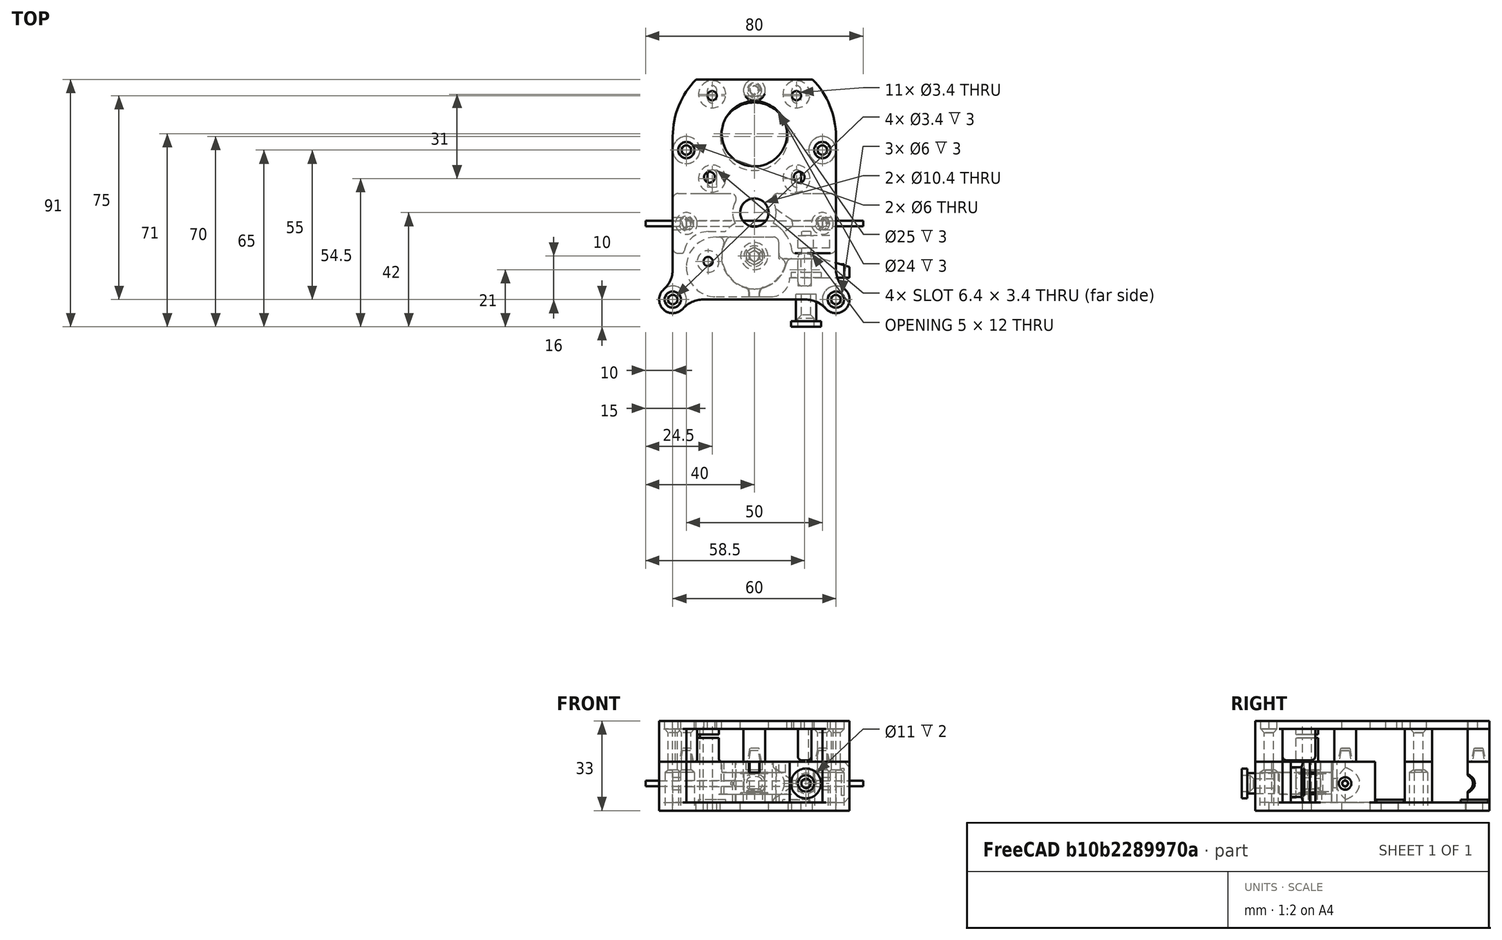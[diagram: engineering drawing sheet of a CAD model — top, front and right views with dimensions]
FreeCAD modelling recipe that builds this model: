
FCSTD DOCUMENT  (FreeCAD 0.14R3700 (Git))
Label: Extruder
License: CC-BY 3.0
LicenseURL: http://creativecommons.org/licenses/by/3.0/
objects: Part::Cylinder×75, Part::Cut×45, Part::MultiFuse×24, Part::Box×20, Part::Cone×12, Mesh::Feature×11, Part::Fillet×7, Part::Chamfer×6, PartDesign::Pad×5, Part::Wedge×2, Sketcher::SketchObject×1
note: 202 computed .brp shape members not serialized (recipe doc carries the construction recipe); baked Part::Feature solids carry a one-line shape summary decoded from their .brp

FEATURE [Part::Box] Box  label="DeltaCubeNema17"
  Height = 3
  Length = 44
  Placement = pos=(-22,21,0) rot=(0,0,1;0rad)
  Width = 10
FEATURE [Part::Cylinder] Cylinder012  label="DeltaCylinderSmallGearTop"
  Angle = 360
  Height = 3
  Placement = pos=(0,1,30) rot=(0,0,1;0rad)
  Radius = 12
FEATURE [Part::Cylinder] Cylinder015
  Angle = 360
  Height = 20
  Placement = pos=(15.5,14,0) rot=(0,0,1;0rad)
  Radius = 1.7
FEATURE [Part::Cylinder] Cylinder016
  Angle = 360
  Height = 20
  Placement = pos=(-15.5,-17,0) rot=(0,0,1;0rad)
  Radius = 1.7
FEATURE [Part::Cylinder] Cylinder017
  Angle = 360
  Height = 20
  Placement = pos=(15.5,-14,0) rot=(0,0,1;0rad)
  Radius = 1.7
FEATURE [Part::Box] Box004  label="Cube"
  Height = 20
  Length = 3.4
  Placement = pos=(13.8,14,0) rot=(0,0,1;0rad)
  Width = 3
FEATURE [Part::Box] Box005  label="Cube051"
  Height = 20
  Length = 3.4
  Placement = pos=(-17.2,-17,0) rot=(0,0,1;0rad)
  Width = 3
FEATURE [Part::Box] Box006  label="Cube052"
  Height = 20
  Length = 3.4
  Placement = pos=(-17.2,14,0) rot=(0,0,1;0rad)
  Width = 3
FEATURE [Part::Box] Box007  label="Cube053"
  Height = 20
  Length = 3.4
  Placement = pos=(13.8,-17,0) rot=(0,0,1;0rad)
  Width = 3
FEATURE [Part::Cylinder] Cylinder018
  Angle = 360
  Height = 20
  Placement = pos=(-15.5,17,0) rot=(0,0,1;0rad)
  Radius = 1.7
FEATURE [Part::Cylinder] Cylinder019
  Angle = 360
  Height = 20
  Placement = pos=(15.5,17,0) rot=(0,0,1;0rad)
  Radius = 1.7
FEATURE [Part::Cylinder] Cylinder020
  Angle = 360
  Height = 20
  Placement = pos=(-15.5,-14,0) rot=(0,0,1;0rad)
  Radius = 1.7
FEATURE [Part::Cylinder] Cylinder021
  Angle = 360
  Height = 20
  Placement = pos=(15.5,-17,0) rot=(0,0,1;0rad)
  Radius = 1.7
FEATURE [Part::Box] Box008  label="CubeBaseTop"
  Height = 3
  Length = 60
  Placement = pos=(-30,-60,30) rot=(0,0,1;0rad)
  Width = 60
FEATURE [Part::Cylinder] Cylinder034  label="DO_NOT_PRINT-Filament"
  Angle = 360
  Height = 80
  Placement = pos=(-40,-32,10) rot=(0,1,0;1.5708rad)
  Radius = 1
FEATURE [Part::Box] Box009  label="PressureCube"
  Height = 15
  Length = 50
  Placement = pos=(-25,-59,3) rot=(0,0,1;0rad)
  Width = 22
FEATURE [Part::Box] Box011  label="FilementHolder"
  Height = 15
  Length = 60
  Placement = pos=(-30,-43,3) rot=(0,0,1;0rad)
  Width = 22
FEATURE [Part::Box] Box012  label="DeltaCube"
  Height = 15
  Length = 16
  Placement = pos=(9,-45,3) rot=(0,0,1;0rad)
  Width = 9
FEATURE [Part::Cylinder] Cylinder040  label="DeltaCylinderSpringPocket"
  Angle = 360
  Height = 2
  Placement = pos=(19,-50,10) rot=(1,0,0;1.5708rad)
  Radius = 5.5
FEATURE [Part::Cylinder] Cylinder041  label="DeltaCylinderSpringNutM4"
  Angle = 360
  Height = 7
  Placement = pos=(19,-45,10) rot=(1,0,0;1.5708rad)
  Radius = 2
FEATURE [Part::Box] Box013  label="DeltaCube001"
  Height = 11
  Length = 5.8
  Placement = pos=(16,-41,7) rot=(0,0,1;0rad)
  Width = 4.5
FEATURE [Part::Cylinder] Cylinder042  label="DeltaCylinder002"
  Angle = 360
  Height = 12
  Placement = pos=(19,-35,10) rot=(1,0,0;1.5708rad)
  Radius = 1.7
FEATURE [Part::Cylinder] Cylinder044  label="DeltaCylinderBearing"
  Angle = 360
  Height = 12
  Placement = pos=(0,-44,6) rot=(0,0,1;0rad)
  Radius = 12.1
FEATURE [Part::Cylinder] Cylinder045  label="CylinderBearingID"
  Angle = 360
  Height = 10.7
  Placement = pos=(0,-44,3) rot=(0,0,1;0rad)
  Radius = 3.8
FEATURE [Part::Cylinder] Cylinder046  label="CylinderBearingBottom"
  Angle = 360
  Height = 0.5
  Placement = pos=(0,-44,6) rot=(0,0,1;0rad)
  Radius = 5
FEATURE [Part::Box] Box014  label="DeltaCubeNema17Top"
  Height = 3
  Length = 44
  Placement = pos=(-22,21,30) rot=(0,0,1;0rad)
  Width = 10
FEATURE [Part::Cylinder] Cylinder047  label="Cylinder043"
  Angle = 360
  Height = 18
  Placement = pos=(30,-60,0) rot=(0,0,-1;0.785398rad)
  Radius = 5
FEATURE [Part::Cylinder] Cylinder048  label="Cylinder044"
  Angle = 360
  Height = 18
  Placement = pos=(-30,-60,0) rot=(0,0,1;3.92699rad)
  Radius = 5
FEATURE [Part::Cylinder] Cylinder049  label="Cylinder045"
  Angle = 360
  Height = 18
  Placement = pos=(25,-5,0) rot=(0,0,1;0rad)
  Radius = 5
FEATURE [Part::Cylinder] Cylinder050  label="Cylinder046"
  Angle = 360
  Height = 18
  Placement = pos=(-25,-5,0) rot=(0,0,1;0rad)
  Radius = 5
FEATURE [Part::Cylinder] Cylinder051  label="AlignmentCylinderNema17"
  Angle = 360
  Height = 18
  Placement = pos=(0,17,0) rot=(0,0,1;0rad)
  Radius = 4
FEATURE [Part::Cylinder] Cylinder052  label="DeltaCylinder005"
  Angle = 360
  Height = 3
  Placement = pos=(30,-60,30) rot=(0,0,1;0rad)
  Radius = 3
FEATURE [Part::Cylinder] Cylinder053  label="DeltaCylinder006"
  Angle = 360
  Height = 3
  Placement = pos=(-30,-60,30) rot=(0,0,1;0rad)
  Radius = 3
FEATURE [Part::Cylinder] Cylinder054  label="DeltaCylinder007"
  Angle = 360
  Height = 3
  Placement = pos=(25,-5,30) rot=(0,0,1;0rad)
  Radius = 3
FEATURE [Part::Cylinder] Cylinder055  label="DeltaCylinder008"
  Angle = 360
  Height = 3
  Placement = pos=(-25,-5,30) rot=(0,0,1;0rad)
  Radius = 3
FEATURE [Part::Cylinder] Cylinder056  label="Cylinder048"
  Angle = 360
  Height = 15
  Placement = pos=(30,-60,18) rot=(0,0,-1;0.785398rad)
  Radius = 5
FEATURE [Part::Cylinder] Cylinder057  label="Cylinder049"
  Angle = 360
  Height = 15
  Placement = pos=(-30,-60,18) rot=(0,0,1;3.75246rad)
  Radius = 5
FEATURE [Part::Cylinder] Cylinder058  label="Cylinder050"
  Angle = 360
  Height = 15
  Placement = pos=(25,-5,18) rot=(0,0,1;0rad)
  Radius = 5
FEATURE [Part::Cylinder] Cylinder059  label="Cylinder051"
  Angle = 360
  Height = 15
  Placement = pos=(-25,-5,18) rot=(0,0,1;0rad)
  Radius = 5
FEATURE [Part::Cylinder] Cylinder060  label="Cylinder052"
  Angle = 360
  Height = 15
  Placement = pos=(0,17,18) rot=(0,0,1;0rad)
  Radius = 4
FEATURE [Part::Cylinder] Cylinder061  label="CylinderBaseBottom"
  Angle = 360
  Height = 3
  Radius = 30
FEATURE [Part::Cylinder] Cylinder062  label="CylinderBaseTop"
  Angle = 360
  Height = 3
  Placement = pos=(0,0,30) rot=(0,0,1;0rad)
  Radius = 30
FEATURE [Part::Cylinder] Cylinder065  label="DeltaCylinder010"
  Angle = 360
  Height = 15
  Placement = pos=(-17,-44,3) rot=(0,0,1;0rad)
  Radius = 9
FEATURE [Part::Cylinder] Cylinder066  label="DeltaCylinder011"
  Angle = 360
  Height = 15
  Placement = pos=(0,-44,3) rot=(0,0,1;0rad)
  Radius = 14
FEATURE [Part::Cylinder] Cylinder067  label="DeltaCylinder012"
  Angle = 360
  Height = 15
  Placement = pos=(0,-28,3) rot=(0,0,1;0rad)
  Radius = 8
FEATURE [Part::Box] Box015  label="DeltaBox"
  Height = 15
  Length = 17
  Placement = pos=(-17,-43,3) rot=(0,0,1;0rad)
  Width = 8
FEATURE [Part::Cut] Cut028
  Base = -> Box011
  Tool = -> Cylinder067
FEATURE [Part::Cut] Cut029
  Base = -> Cut028
  Tool = -> Cylinder066
FEATURE [Part::Cut] Cut030
  Base = -> Cut029
  Tool = -> Cylinder065
FEATURE [Part::Cut] Cut031
  Base = -> Cut030
  Tool = -> Box015
FEATURE [Part::Cut] Cut032
  Base = -> Cut031
  Tool = -> Box013
FEATURE [Part::Cut] Cut033
  Base = -> Cut032
  Tool = -> Cylinder042
FEATURE [Part::Cylinder] Cylinder068  label="DeltaCylinder013"
  Angle = 360
  Height = 80
  Placement = pos=(-40,-32,10) rot=(0,1,0;1.5708rad)
  Radius = 1.1
FEATURE [Part::Cut] Cut034
  Base = -> Cut033
  Tool = -> Cylinder068
FEATURE [Part::Fillet] Fillet002
  Base = -> Cut034
  Edges = 6 edges r=2: [Edge1,Edge4,Edge19,Edge30,Edge44,Edge57]
FEATURE [Part::Fillet] Fillet003
  Base = -> Fillet002
  Edges = 3 edges r=1: [Edge34,Edge35,Edge39]
FEATURE [Part::Cylinder] Cylinder070  label="DeltaCylinder014"
  Angle = 360
  Height = 5
  Placement = pos=(-30,-32,10) rot=(0,1,0;1.5708rad)
  Radius = 2.3
FEATURE [Part::Cylinder] Cylinder071  label="DeltaCylinder015"
  Angle = 360
  Height = 5
  Placement = pos=(25,-32,10) rot=(0,1,0;1.5708rad)
  Radius = 2.3
FEATURE [Part::Cut] Cut035
  Base = -> Fillet003
  Tool = -> Cylinder070
FEATURE [Part::Cut] Cut036
  Base = -> Cut035
  Tool = -> Cylinder071
FEATURE [Part::Cone] Cone  label="DeltaCone"
  Angle = 360
  Height = 7.1
  Placement = pos=(14,-32,10) rot=(0,-1,0;1.5708rad)
  Radius1 = 1.1
  Radius2 = 6
FEATURE [Part::Cut] Cut037  label="FilamentGuide"
  Base = -> Cut036
  Tool = -> Cone
FEATURE [Part::Cylinder] Cylinder072  label="Cylinder102"
  Angle = 360
  Height = 20
  Placement = pos=(-15.5,14,0) rot=(0,0,1;0rad)
  Radius = 1.7
FEATURE [Part::Cylinder] Cylinder073  label="Cylinder103"
  Angle = 360
  Height = 1
  Placement = pos=(-15.5,15.5,3) rot=(0,0,1;0rad)
  Radius = 5
FEATURE [Part::Cylinder] Cylinder074  label="Cylinder104"
  Angle = 360
  Height = 1
  Placement = pos=(15.5,15.5,3) rot=(0,0,1;0rad)
  Radius = 5
FEATURE [Part::Cylinder] Cylinder075  label="Cylinder105"
  Angle = 360
  Height = 1
  Placement = pos=(-15.5,-15.5,3) rot=(0,0,1;0rad)
  Radius = 5
FEATURE [Part::Cylinder] Cylinder076  label="Cylinder113"
  Angle = 360
  Height = 1
  Placement = pos=(15.5,-15.5,3) rot=(0,0,1;0rad)
  Radius = 5
FEATURE [Part::Cylinder] Cylinder077  label="DeltaCylinderNema17"
  Angle = 360
  Height = 3
  Radius = 12.5
FEATURE [Part::Box] Box016  label="CubeBaseBottom"
  Height = 3
  Length = 60
  Placement = pos=(-30,-60,0) rot=(0,0,1;0rad)
  Width = 60
FEATURE [Mesh::Feature] ExtruderGear
  Placement = pos=(0,-28,5.2) rot=(0,0,1;0rad)
FEATURE [Mesh::Feature] F623ZZ
  Placement = pos=(0,-28,4) rot=(0,1,0;3.14159rad)
FEATURE [Mesh::Feature] ILQ_9  label="ILQ-9"
  Placement = pos=(0,-44,6.5) rot=(0,0,1;0rad)
FEATURE [Mesh::Feature] M3_Washer  label="M3-Washer"
  Placement = pos=(0,-28,4) rot=(0,0,1;0rad)
FEATURE [Mesh::Feature] M3_Washer001  label="M3-Washer001"
  Placement = pos=(0,-28,4.6) rot=(0,0,1;0rad)
FEATURE [Mesh::Feature] M3_Washer002  label="M3-Washer002"
  Placement = pos=(0,-28,27.2) rot=(0,0,1;0rad)
FEATURE [Mesh::Feature] F623ZZ001
  Placement = pos=(0,-28,29) rot=(0,0,1;0rad)
FEATURE [Mesh::Feature] M3_Washer003  label="M3-Washer003"
  Placement = pos=(0,-28,27.8) rot=(0,0,1;0rad)
FEATURE [Mesh::Feature] Nema  label="Nema17"
  Placement = pos=(-28,23,-52) rot=(0,0,1;0rad)
FEATURE [Part::Cylinder] Cylinder  label="DeltaCylinder018"
  Angle = 360
  Height = 15
  Placement = pos=(-30,-60,18) rot=(0,0,1;0rad)
  Radius = 1.7
FEATURE [Part::Cylinder] Cylinder078  label="DeltaCylinder019"
  Angle = 360
  Height = 15
  Placement = pos=(30,-60,18) rot=(0,0,1;0rad)
  Radius = 1.7
FEATURE [Part::Cylinder] Cylinder079  label="DeltaCylinder020"
  Angle = 360
  Height = 15
  Placement = pos=(25,-5,18) rot=(0,0,1;0rad)
  Radius = 1.7
FEATURE [Part::Cylinder] Cylinder080  label="DeltaCylinder021"
  Angle = 360
  Height = 15
  Placement = pos=(-25,-5,18) rot=(0,0,1;0rad)
  Radius = 1.7
FEATURE [Part::Cylinder] Cylinder081  label="DeltaCylinder022"
  Angle = 360
  Height = 18
  Placement = pos=(30,-60,0) rot=(0,0,1;0rad)
  Radius = 1.7
FEATURE [Part::Cylinder] Cylinder082  label="DeltaCylinder023"
  Angle = 360
  Height = 18
  Placement = pos=(-30,-60,0) rot=(0,0,1;0rad)
  Radius = 1.7
FEATURE [Part::Cylinder] Cylinder083  label="DeltaCylinder024"
  Angle = 360
  Height = 18
  Placement = pos=(-25,-5,0) rot=(0,0,1;0rad)
  Radius = 1.7
FEATURE [Part::Cylinder] Cylinder084  label="DeltaCylinder025"
  Angle = 360
  Height = 18
  Placement = pos=(25,-5,0) rot=(0,0,1;0rad)
  Radius = 1.7
FEATURE [Part::Cylinder] Cylinder085  label="DeltaCylinderF623ZZBottom"
  Angle = 360
  Height = 3
  Placement = pos=(0,-28,0) rot=(0,0,1;0rad)
  Radius = 5.2
FEATURE [Part::Cylinder] Cylinder086  label="DeltaCylinderF623ZZTop"
  Angle = 360
  Height = 3
  Placement = pos=(0,-28,30) rot=(0,0,1;0rad)
  Radius = 5.2
FEATURE [Part::Cone] Cone001  label="AlignmentConeBottom"
  Angle = 360
  Height = 4
  Placement = pos=(0,17,18) rot=(0,0,1;0rad)
  Radius1 = 2.25
  Radius2 = 1.5
FEATURE [Part::Cone] Cone002  label="DeltaConeTop"
  Angle = 360
  Height = 5
  Placement = pos=(0,17,18) rot=(0,0,1;0rad)
  Radius1 = 2.7
  Radius2 = 1.7
FEATURE [Part::Cylinder] Cylinder087  label="Cylinder114"
  Angle = 360
  Height = 15
  Placement = pos=(25,-32,18) rot=(0,0,1;0rad)
  Radius = 4
FEATURE [Part::Cylinder] Cylinder088  label="Cylinder115"
  Angle = 360
  Height = 15
  Placement = pos=(-25,-32,18) rot=(0,0,1;0rad)
  Radius = 4
FEATURE [Part::Cone] Cone003  label="AlignmentConeBottom001"
  Angle = 360
  Height = 4
  Placement = pos=(-25,-32,18) rot=(0,0,1;0rad)
  Radius1 = 2.25
  Radius2 = 1.5
FEATURE [Part::Cone] Cone004  label="AlignmentConeBottom002"
  Angle = 360
  Height = 4
  Placement = pos=(25,-32,18) rot=(0,0,1;0rad)
  Radius1 = 2.25
  Radius2 = 1.5
FEATURE [Part::Cone] Cone005  label="DeltaConeTop001"
  Angle = 360
  Height = 5
  Placement = pos=(-25,-32,18) rot=(0,0,1;0rad)
  Radius1 = 2.7
  Radius2 = 1.7
FEATURE [Part::Cone] Cone006  label="DeltaConeTop002"
  Angle = 360
  Height = 5
  Placement = pos=(25,-32,18) rot=(0,0,1;0rad)
  Radius1 = 2.7
  Radius2 = 1.7
FEATURE [Part::Wedge] Wedge  label="WedgeFinger"
  Placement = pos=(25,-52,3) rot=(-0.57735,-0.57735,-0.57735;2.0944rad)
  X2max = 15
  X2min = 0
  Xmax = 15
  Xmin = 0
  Ymax = 10
  Ymin = 0
  Z2max = 4
  Z2min = 0
  Zmax = 7
  Zmin = 0
FEATURE [Part::Cylinder] Cylinder089  label="DeltaCylinderBearingM3"
  Angle = 360
  Height = 10
  Placement = pos=(0,-44,5) rot=(0,0,1;0rad)
  Radius = 1.7
FEATURE [Part::Box] Box017  label="CubeFingerGrip"
  Height = 10
  Length = 1
  Placement = pos=(32,-49,5.5) rot=(0,0,1;0rad)
  Width = 2
FEATURE [Part::Cylinder] Cylinder090  label="DeltaCylinder029"
  Angle = 360
  Height = 3
  Placement = pos=(16.5,-15,30) rot=(0,0,1;0rad)
  Radius = 2
FEATURE [Part::Cylinder] Cylinder091  label="DeltaCylinder030"
  Angle = 360
  Height = 3
  Placement = pos=(-16.5,-15,30) rot=(0,0,1;0rad)
  Radius = 2
FEATURE [Part::Cylinder] Cylinder092  label="DeltaCylinder031"
  Angle = 360
  Height = 3
  Placement = pos=(-15.5,15,30) rot=(0,0,1;0rad)
  Radius = 1.7
FEATURE [Part::Cylinder] Cylinder093  label="DeltaCylinder032"
  Angle = 360
  Height = 3
  Placement = pos=(15.5,15,30) rot=(0,0,1;0rad)
  Radius = 1.7
FEATURE [Part::Box] Box018  label="Cube061"
  Height = 14.5
  Length = 5
  Placement = pos=(16,-55,18.5) rot=(0,0,1;0rad)
  Width = 12
FEATURE [Sketcher::SketchObject] Sketch  label="SketchNutOutline"
  Placement = pos=(0,0,0) rot=(1,0,0;1.5708rad)
  sketch-geometry (6):
    g0: LineSegment StartX=-2.9 StartY=1.67432 StartZ=0 EndX=-2.9 EndY=-1.67432 EndZ=0
    g1: LineSegment StartX=-2.9 StartY=-1.67432 StartZ=0 EndX=0 EndY=-3.34863 EndZ=0
    g2: LineSegment StartX=0 StartY=-3.34863 StartZ=0 EndX=2.9 EndY=-1.67432 EndZ=0
    g3: LineSegment StartX=2.9 StartY=-1.67432 StartZ=0 EndX=2.9 EndY=1.67432 EndZ=0
    g4: LineSegment StartX=2.9 StartY=1.67432 StartZ=0 EndX=0 EndY=3.34863 EndZ=0
    g5: LineSegment StartX=0 StartY=3.34863 StartZ=0 EndX=-2.9 EndY=1.67432 EndZ=0
  constraints (18):
    c: Vertical(g0)
    c: Coincident(g0,g1)
    c: PointOnObject(g1,g-2)
    c: Coincident(g1,g2)
    c: Coincident(g2,g3)
    c: Vertical(g3)
    c: Coincident(g3,g4)
    c: PointOnObject(g4,g-2)
    c: Coincident(g4,g5)
    c: Coincident(g5,g0)
    c: Equal(g5,g0)
    c: Equal(g0,g1)
    c: Equal(g1,g2)
    c: Equal(g2,g3)
    c: Equal(g3,g4)
    c: Angle(g0,g5) = 2.0944
    c: Symmetric(g4,g1,g-1)
    c: DistanceX(g0,g3) = 5.8
FEATURE [PartDesign::Pad] Pad
  Length = 20
  Length2 = 100
  Placement = pos=(0,0,0) rot=(1,0,0;1.5708rad)
  Sketch = -> Sketch
  Type = 0
FEATURE [Part::Chamfer] Chamfer  label="NutDelta"
  Base = -> Pad
  Edges = 12 edges r=1: [Edge3,Edge4,Edge6,Edge7,Edge9,Edge10,Edge12,Edge13,Edge15,Edge16,Edge17,Edge18]
  Placement = pos=(-30,-60,15) rot=(1,0,0;1.5708rad)
FEATURE [PartDesign::Pad] Pad001
  Length = 20
  Length2 = 100
  Placement = pos=(0,0,0) rot=(1,0,0;1.5708rad)
  Sketch = -> Sketch
  Type = 0
FEATURE [Part::Chamfer] Chamfer001  label="NutDelta001"
  Base = -> Pad001
  Edges = 12 edges r=1: [Edge3,Edge4,Edge6,Edge7,Edge9,Edge10,Edge12,Edge13,Edge15,Edge16,Edge17,Edge18]
  Placement = pos=(30,-60,15) rot=(1,0,0;1.5708rad)
FEATURE [PartDesign::Pad] Pad002
  Length = 20
  Length2 = 100
  Placement = pos=(0,0,0) rot=(1,0,0;1.5708rad)
  Sketch = -> Sketch
  Type = 0
FEATURE [Part::Chamfer] Chamfer002  label="NutDelta002"
  Base = -> Pad002
  Edges = 12 edges r=1: [Edge3,Edge4,Edge6,Edge7,Edge9,Edge10,Edge12,Edge13,Edge15,Edge16,Edge17,Edge18]
  Placement = pos=(25,-5,15) rot=(1,0,0;1.5708rad)
FEATURE [PartDesign::Pad] Pad003
  Length = 20
  Length2 = 100
  Placement = pos=(0,0,0) rot=(1,0,0;1.5708rad)
  Sketch = -> Sketch
  Type = 0
FEATURE [Part::Chamfer] Chamfer003  label="NutDelta003"
  Base = -> Pad003
  Edges = 12 edges r=1: [Edge3,Edge4,Edge6,Edge7,Edge9,Edge10,Edge12,Edge13,Edge15,Edge16,Edge17,Edge18]
  Placement = pos=(0,-44,8) rot=(1,0,0;1.5708rad)
FEATURE [PartDesign::Pad] Pad004
  Length = 20
  Length2 = 100
  Placement = pos=(0,0,0) rot=(1,0,0;1.5708rad)
  Sketch = -> Sketch
  Type = 0
FEATURE [Part::Chamfer] Chamfer004  label="NutDelta004"
  Base = -> Pad004
  Edges = 12 edges r=1: [Edge3,Edge4,Edge6,Edge7,Edge9,Edge10,Edge12,Edge13,Edge15,Edge16,Edge17,Edge18]
  Placement = pos=(-25,-5,15) rot=(1,0,0;1.5708rad)
FEATURE [Part::Cylinder] Cylinder094  label="CylinderBearingHolderTop"
  Angle = 360
  Height = 4
  Placement = pos=(0,-44,14) rot=(0,0,1;0rad)
  Radius = 11.9
FEATURE [Part::Cylinder] Cylinder095  label="DeltaCylinderM3"
  Angle = 360
  Height = 4
  Placement = pos=(0,-44,14) rot=(0,0,1;0rad)
  Radius = 1.7
FEATURE [Part::Cylinder] Cylinder096  label="DeltaCylinderNutHead"
  Angle = 360
  Height = 3
  Placement = pos=(0,-44,15) rot=(0,0,1;0rad)
  Radius = 3
FEATURE [Part::Box] Box019  label="DeltaCube003"
  Height = 4
  Length = 24
  Placement = pos=(-12,-37,14) rot=(0,0,1;0rad)
  Width = 10
FEATURE [Part::Box] Box020  label="DeltaCube004"
  Height = 4
  Length = 24
  Placement = pos=(9,-45,14) rot=(0,0,1;0rad)
  Width = 10
FEATURE [Part::Box] Box021  label="CubeAlignment"
  Height = 4
  Length = 3.6
  Placement = pos=(-1.8,-59,14) rot=(0,0,1;0rad)
  Width = 4
FEATURE [Part::Cylinder] Cylinder097  label="Cylinder116"
  Angle = 360
  Height = 2
  Radius = 5.5
FEATURE [Part::Cylinder] Cylinder098  label="Cylinder117"
  Angle = 360
  Height = 10
  Placement = pos=(0,0,2) rot=(0,0,1;0rad)
  Radius = 3.75
FEATURE [Part::Cylinder] Cylinder099  label="DeltaCylinder035"
  Angle = 360
  Height = 3
  Radius = 3
FEATURE [Part::Cylinder] Cylinder100  label="DeltaCylinder036"
  Angle = 360
  Height = 12
  Radius = 1.7
FEATURE [Part::Cone] Cone007  label="DeltaCone001"
  Angle = 360
  Height = 1.3
  Placement = pos=(0,0,3) rot=(0,0,1;0rad)
  Radius1 = 3
  Radius2 = 1.7
FEATURE [Part::MultiFuse] Fusion004
  Shapes = -> [Cylinder097,Cylinder098]
FEATURE [Part::Cut] Cut049
  Base = -> Fusion004
  Tool = -> Cone007
FEATURE [Part::Cut] Cut050
  Base = -> Cut049
  Tool = -> Cylinder099
FEATURE [Part::Cut] Cut051  label="SpringGuide"
  Base = -> Cut050
  Placement = pos=(19,-70,10) rot=(-1,0,0;1.5708rad)
  Tool = -> Cylinder100
FEATURE [Part::MultiFuse] Fusion006  label="DeltaVariableNutBottom"
  Shapes = -> [Box006,Cylinder072,Cylinder018]
FEATURE [Part::MultiFuse] Fusion007  label="DeltaVariableNutBottom001"
  Shapes = -> [Box004,Cylinder015,Cylinder019]
FEATURE [Part::MultiFuse] Fusion008  label="DeltaVariableNutBottom002"
  Shapes = -> [Box007,Cylinder021,Cylinder017]
FEATURE [Part::MultiFuse] Fusion009  label="DeltaVariableNutBottom003"
  Shapes = -> [Box005,Cylinder016,Cylinder020]
FEATURE [Part::Cylinder] Cylinder101  label="DeltaCylinderSmallGearTighteningScrew"
  Angle = 360
  Height = 10
  Placement = pos=(-5,12,10) rot=(0,1,0;1.5708rad)
  Radius = 3
FEATURE [Part::MultiFuse] Fusion018  label="DeltaNylonNutFusion"
  Shapes = -> [Chamfer004,Chamfer002,Chamfer001,Chamfer]
FEATURE [Part::MultiFuse] Fusion019  label="DeltaCylinderM3Bottom"
  Shapes = -> [Cylinder081,Cylinder083,Cylinder084,Cylinder082]
FEATURE [Part::MultiFuse] Fusion020  label="DeltaVariableNutFusionBottom"
  Shapes = -> [Fusion009,Fusion008,Fusion007,Fusion006]
FEATURE [Part::MultiFuse] Fusion021  label="AlignmentBoltsBottom"
  Shapes = -> [Cone001,Cone003,Cone004]
FEATURE [Part::MultiFuse] Fusion022  label="NutDistanceNema17"
  Shapes = -> [Cylinder075,Cylinder073,Cylinder074,Cylinder076]
FEATURE [Part::MultiFuse] Fusion023  label="NutCylindersBottom"
  Shapes = -> [Cylinder048,Cylinder049,Cylinder047,Cylinder050]
FEATURE [Part::MultiFuse] Fusion025  label="DeltaCylinderNemaHexNut"
  Shapes = -> [Cylinder093,Cylinder092,Cylinder091,Cylinder090]
FEATURE [Part::MultiFuse] Fusion026  label="DeltaAlignmentBoltsTop"
  Shapes = -> [Cone006,Cone005,Cone002]
FEATURE [Part::MultiFuse] Fusion027  label="DeltaCylinderM3Top"
  Shapes = -> [Cylinder080,Cylinder079,Cylinder078,Cylinder]
FEATURE [Part::MultiFuse] Fusion028  label="DeltaCylinderNutHeadsTop"
  Shapes = -> [Cylinder055,Cylinder054,Cylinder053,Cylinder052]
FEATURE [Part::MultiFuse] Fusion029  label="CylinderAlignmentBoltsTop"
  Shapes = -> [Cylinder060,Cylinder087,Cylinder088]
FEATURE [Part::MultiFuse] Fusion030  label="CylinderNutsTop"
  Shapes = -> [Cylinder059,Cylinder057,Cylinder056,Cylinder058]
FEATURE [Part::Fillet] Fillet011  label="SlidingBoxTop"
  Base = -> Box018
  Edges = 8 edges r=1.5: [Edge1,Edge3,Edge4,Edge5,Edge7,Edge8,Edge9,Edge11]
FEATURE [Part::Cylinder] Cylinder106  label="CylinderHolderWasherTop"
  Angle = 360
  Height = 2
  Placement = pos=(-17,-46,28) rot=(0,0,1;0rad)
  Radius = 4
FEATURE [Part::Cylinder] Cylinder107  label="DeltaCylinderHolderAxisTop"
  Angle = 360
  Height = 5
  Placement = pos=(-17,-46,28) rot=(0,0,1;0rad)
  Radius = 1.7
FEATURE [Part::Cylinder] Cylinder108  label="BearingHolderDistanceTop"
  Angle = 360
  Height = 8.8
  Placement = pos=(-17,-46,18) rot=(0,0,1;0rad)
  Radius = 4
FEATURE [Part::Cylinder] Cylinder109  label="DeltaCylinderM3RotationAxis"
  Angle = 360
  Height = 23.8
  Placement = pos=(-17,-46,3) rot=(0,0,1;0rad)
  Radius = 1.7
FEATURE [Part::Box] Box023  label="DeltaCube006"
  Height = 4
  Length = 4
  Placement = pos=(-2,-59,14) rot=(0,0,1;0rad)
  Width = 4
FEATURE [Part::Cone] Cone008  label="DeltaCone002"
  Angle = 360
  Height = 1.3
  Placement = pos=(25,-5,28.7) rot=(0,0,1;0rad)
  Radius1 = 1.7
  Radius2 = 3
FEATURE [Part::Cone] Cone009  label="DeltaCone003"
  Angle = 360
  Height = 1.3
  Placement = pos=(-25,-5,28.7) rot=(0,0,1;0rad)
  Radius1 = 1.7
  Radius2 = 3
FEATURE [Part::Cone] Cone010  label="DeltaCone004"
  Angle = 360
  Height = 1.3
  Placement = pos=(-30,-60,28.7) rot=(0,0,1;0rad)
  Radius1 = 1.7
  Radius2 = 3
FEATURE [Part::Cone] Cone011  label="DeltaCone005"
  Angle = 360
  Height = 1.3
  Placement = pos=(30,-60,28.7) rot=(0,0,1;0rad)
  Radius1 = 1.7
  Radius2 = 3
FEATURE [Part::MultiFuse] Fusion031  label="DeltaConeNutHeadsTop"
  Shapes = -> [Cone008,Cone011,Cone010,Cone009]
FEATURE [Part::Box] Box024  label="DeltaCube007"
  Height = 15
  Length = 12
  Placement = pos=(13,-59,3) rot=(0,0,1;0rad)
  Width = 7
FEATURE [Part::MultiFuse] Fusion033
  Shapes = -> [Cylinder094,Box021]
FEATURE [Part::Cut] Cut
  Base = -> Fusion033
  Tool = -> Box020
FEATURE [Part::Cut] Cut052
  Base = -> Cut
  Tool = -> Box019
FEATURE [Part::Cut] Cut053
  Base = -> Cut052
  Tool = -> Cylinder095
FEATURE [Part::Cut] Cut054
  Base = -> Cut053
  Tool = -> Cylinder096
FEATURE [Part::Fillet] Fillet  label="BearingHolderTop"
  Base = -> Cut054
  Edges = 5 edges r=2: [Edge9,Edge12,Edge16,Edge24,Edge34]
FEATURE [Part::Cylinder] Cylinder110  label="DeltaCylinderWasherM3"
  Angle = 360
  Height = 0.5
  Placement = pos=(0,-44,13.5) rot=(0,0,1;0rad)
  Radius = 1.7
FEATURE [Part::Cylinder] Cylinder111  label="CylinderWasher"
  Angle = 360
  Height = 0.5
  Placement = pos=(0,-44,13.5) rot=(0,0,1;0rad)
  Radius = 5
FEATURE [Part::Cut] Cut055  label="BearingHolderTopWasher"
  Base = -> Cylinder111
  Tool = -> Cylinder110
FEATURE [Part::MultiFuse] Fusion  label="FusionBearingCylinder"
  Shapes = -> [Cylinder046,Cylinder045]
FEATURE [Part::MultiFuse] Fusion034  label="FusionBasePartsForCuts"
  Shapes = -> [Box017,Wedge,Box009]
FEATURE [Part::Cut] Cut056
  Base = -> Fusion034
  Tool = -> Box024
FEATURE [Part::Cut] Cut057
  Base = -> Cut056
  Tool = -> Cylinder044
FEATURE [Part::Cut] Cut058
  Base = -> Cut057
  Tool = -> Box012
FEATURE [Part::Cut] Cut059
  Base = -> Cut058
  Tool = -> Cylinder040
FEATURE [Part::Cut] Cut060
  Base = -> Cut059
  Tool = -> Cylinder041
FEATURE [Part::MultiFuse] Fusion035
  Shapes = -> [Fusion,Cut060,Cylinder108]
FEATURE [Part::Cut] Cut061
  Base = -> Fusion035
  Tool = -> Cylinder109
FEATURE [Part::Cut] Cut062
  Base = -> Cut061
  Tool = -> Box023
FEATURE [Part::Cut] Cut063
  Base = -> Cut062
  Tool = -> Chamfer003
FEATURE [Part::Cut] Cut064
  Base = -> Cut063
  Tool = -> Cylinder089
FEATURE [Part::Fillet] Fillet012
  Base = -> Cut064
  Edges = 10 edges: [Edge4 r=1,Edge21 r=2,Edge23 r=2,Edge24 r=10.95,Edge26 r=2,Edge28 r=2,Edge30 r=2,Edge33 r=6.95,Edge37 r=10.95,Edge38 r=2]
FEATURE [Part::Chamfer] Chamfer005  label="BearingHolderBottom"
  Base = -> Fillet012
  Edges = 2 edges r=2: [Edge85,Edge99]
FEATURE [Part::Cylinder] Cylinder112  label="DeltaCylinderBearingHolderAxisM3"
  Angle = 360
  Height = 3
  Placement = pos=(-17,-46,0) rot=(0,0,1;0rad)
  Radius = 1.7
FEATURE [Part::MultiFuse] Fusion036  label="FusionBaseBottom"
  Shapes = -> [Cylinder051,Cylinder061,Box016,Cut037,Fusion023,Fusion022,Fusion021]
FEATURE [Part::Cut] Cut065
  Base = -> Fusion036
  Tool = -> Cylinder112
FEATURE [Part::Cut] Cut066
  Base = -> Cut065
  Tool = -> Cylinder101
FEATURE [Part::Cut] Cut067
  Base = -> Cut066
  Tool = -> Cylinder085
FEATURE [Part::Cut] Cut068
  Base = -> Cut067
  Tool = -> Fusion018
FEATURE [Part::Cut] Cut069
  Base = -> Cut068
  Tool = -> Fusion019
FEATURE [Part::Cut] Cut070
  Base = -> Cut069
  Tool = -> Fusion020
FEATURE [Part::Cut] Cut071
  Base = -> Cut070
  Tool = -> Cylinder077
FEATURE [Part::Cut] Cut072
  Base = -> Cut071
  Tool = -> Box
FEATURE [Part::Fillet] Fillet013  label="Chamfer"
  Base = -> Cut072
  Edges = 5 edges: [Edge75 r=10,Edge78 r=10,Edge82 r=10,Edge85 r=10,Edge238 r=1]
FEATURE [Part::MultiFuse] Fusion037  label="FusionBaseTop"
  Shapes = -> [Box008,Cylinder062,Fillet011,Fusion029,Fusion030,Cylinder106]
FEATURE [Part::Cut] Cut073
  Base = -> Fusion037
  Tool = -> Fusion025
FEATURE [Part::Cut] Cut074
  Base = -> Cut073
  Tool = -> Cylinder012
FEATURE [Part::Cut] Cut075
  Base = -> Cut074
  Tool = -> Box014
FEATURE [Part::Cut] Cut076
  Base = -> Cut075
  Tool = -> Cylinder086
FEATURE [Part::Cut] Cut077
  Base = -> Cut076
  Tool = -> Cylinder107
FEATURE [Part::Cut] Cut078
  Base = -> Cut077
  Tool = -> Fusion031
FEATURE [Part::Cut] Cut079
  Base = -> Cut078
  Tool = -> Fusion026
FEATURE [Part::Cut] Cut080
  Base = -> Cut079
  Tool = -> Fusion027
FEATURE [Part::Cut] Cut081
  Base = -> Cut080
  Tool = -> Fusion028
FEATURE [Part::Fillet] Fillet014  label="ExtruderCaseTop"
  Base = -> Cut081
  Edges = 4 edges r=10: [Edge69,Edge73,Edge75,Edge79]
FEATURE [Mesh::Feature] BigGear
  Placement = pos=(0,0,27.2) rot=(0,1,0;3.14159rad)
FEATURE [Mesh::Feature] SmallGear
  Placement = pos=(0,0,43) rot=(0,0,1;0rad)
FEATURE [Part::Wedge] Wedge001  label="DeltaWedge"
  Placement = pos=(27.75,-41,12) rot=(0,0,1;1.5708rad)
  X2max = 4.5
  X2min = 0
  Xmax = 4.5
  Xmin = 0
  Ymax = 6
  Ymin = 0
  Z2max = 6
  Z2min = 2
  Zmax = 6
  Zmin = 5.99
FEATURE [Part::Cut] Cut082  label="ExtruderCaseBottom"
  Base = -> Fillet013
  Tool = -> Wedge001
